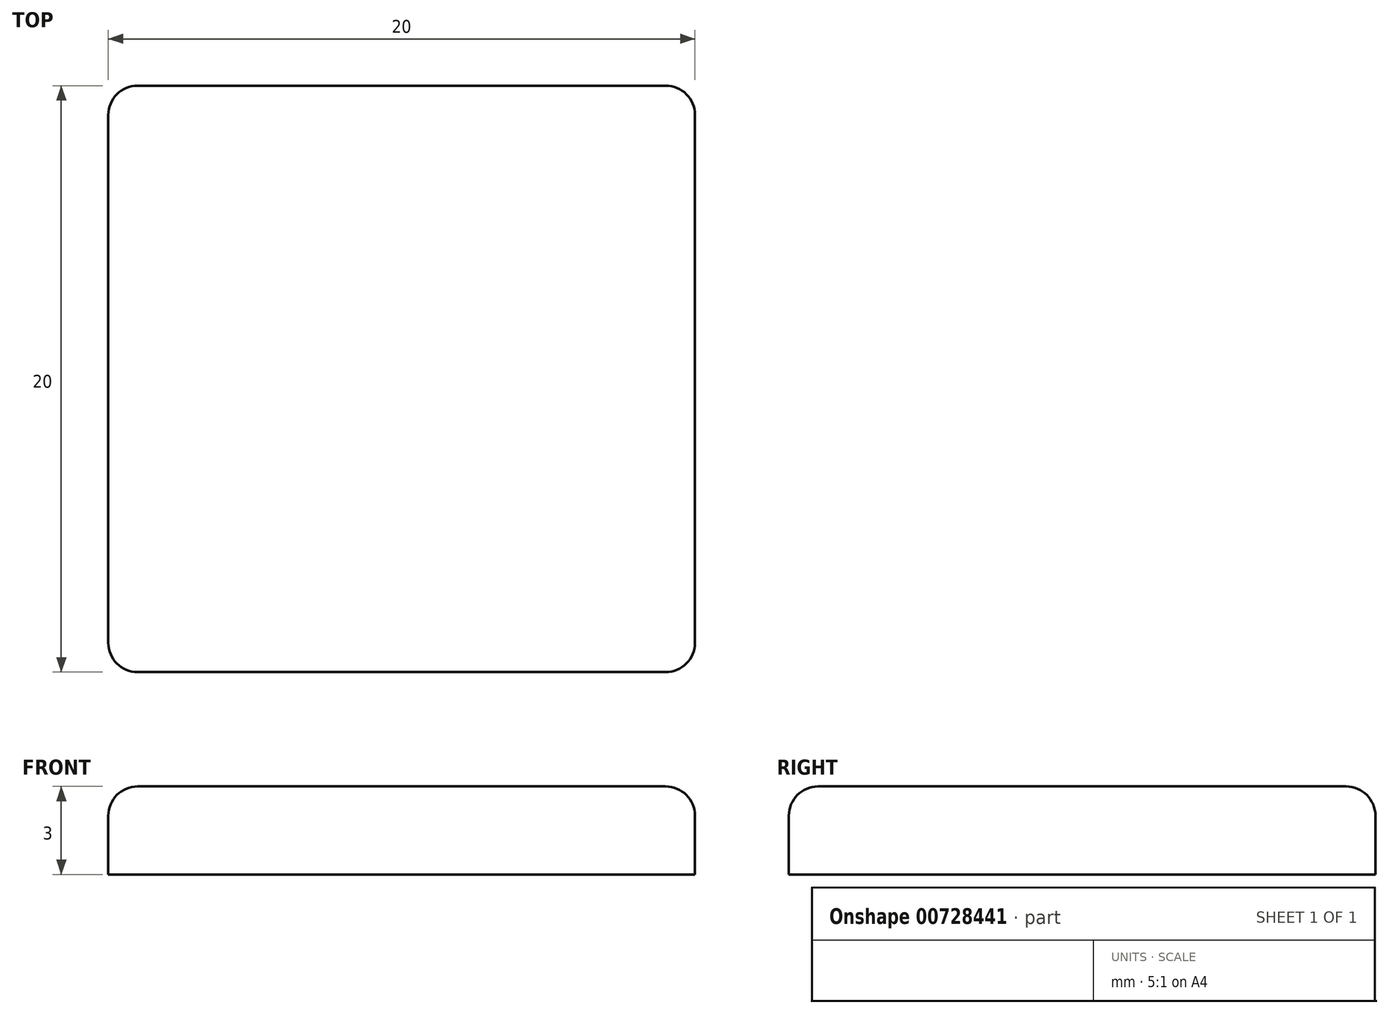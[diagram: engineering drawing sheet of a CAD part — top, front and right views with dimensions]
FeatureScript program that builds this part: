
annotation { "Feature Type Name" : "Feature", "Feature Type Description" : "" }
export const myFeature = defineFeature(function(context is Context, id is Id, definition is map)
    precondition{}
    {
        {
            var Q0;
            Q0=qCreatedBy(makeId("Top.planeOp"),FACE);
            var sketch = newSketch(context, id + "F0", { "sketchPlane" : qUnion([Q0])});
            skLineSegment(sketch, "E0.bottom", {"start": v(-10, 10) * mm, "end": v(10, 10) * mm});
            skLineSegment(sketch, "E0.top", {"start": v(-10, -10) * mm, "end": v(10, -10) * mm});
            skLineSegment(sketch, "E0.left", {"start": v(-10, 10) * mm, "end": v(-10, -10) * mm});
            skLineSegment(sketch, "E0.right", {"start": v(10, 10) * mm, "end": v(10, -10) * mm});
            skPoint(sketch, "E0.middle", {"position": v(0, 0) * mm});
            skSolve(sketch);
        }
        {
            var Q0;
            Q0=makeQuery(id+"F0.imprint","IMPRINT",FACE,{"disambiguationData":[TD([[makeQuery(id+"F0.imprint","IMPRINT",EDGE,{"derivedFrom":sQuery(id+"F0.wireOp",EDGE,"E0.bottom")}),-1.0]])]});
            extrude(context, id + "F1", {"entities" : qUnion([Q0]), "depth" : 3 * mm, "offsetDistance" : 25 * mm});
        }
        {
            var Q0;
            Q0=makeQuery(id+"F1.opExtrude","CAP_FACE",FACE,{"disambiguationData":[OSD([sQuery(id+"F0.wireOp",EDGE,"E0.bottom"),sQuery(id+"F0.wireOp",EDGE,"E0.top"),sQuery(id+"F0.wireOp",EDGE,"E0.left"),sQuery(id+"F0.wireOp",EDGE,"E0.right")])],"isStart":false});
            var Q1;
            Q1=makeQuery(id+"F1.opExtrude","SWEPT_EDGE",EDGE,{"disambiguationData":[OSD([sQuery(id+"F0.wireOp",EDGE,"E0.top"),sQuery(id+"F0.wireOp",EDGE,"E0.left")])]});
            var Q2;
            Q2=makeQuery(id+"F1.opExtrude","SWEPT_EDGE",EDGE,{"disambiguationData":[OSD([sQuery(id+"F0.wireOp",EDGE,"E0.bottom"),sQuery(id+"F0.wireOp",EDGE,"E0.left")])]});
            var Q3;
            Q3=makeQuery(id+"F1.opExtrude","SWEPT_EDGE",EDGE,{"disambiguationData":[OSD([sQuery(id+"F0.wireOp",EDGE,"E0.top"),sQuery(id+"F0.wireOp",EDGE,"E0.right")])]});
            var Q4;
            Q4=makeQuery(id+"F1.opExtrude","SWEPT_EDGE",EDGE,{"disambiguationData":[OSD([sQuery(id+"F0.wireOp",EDGE,"E0.bottom"),sQuery(id+"F0.wireOp",EDGE,"E0.right")])]});
            fillet(context, id + "F2", {"entities" : qUnion([Q0, Q1, Q2, Q3, Q4]), "radius" : 1 * mm, "tangentPropagation" : true, "allowEdgeOverflow" : false});
        }
    });
